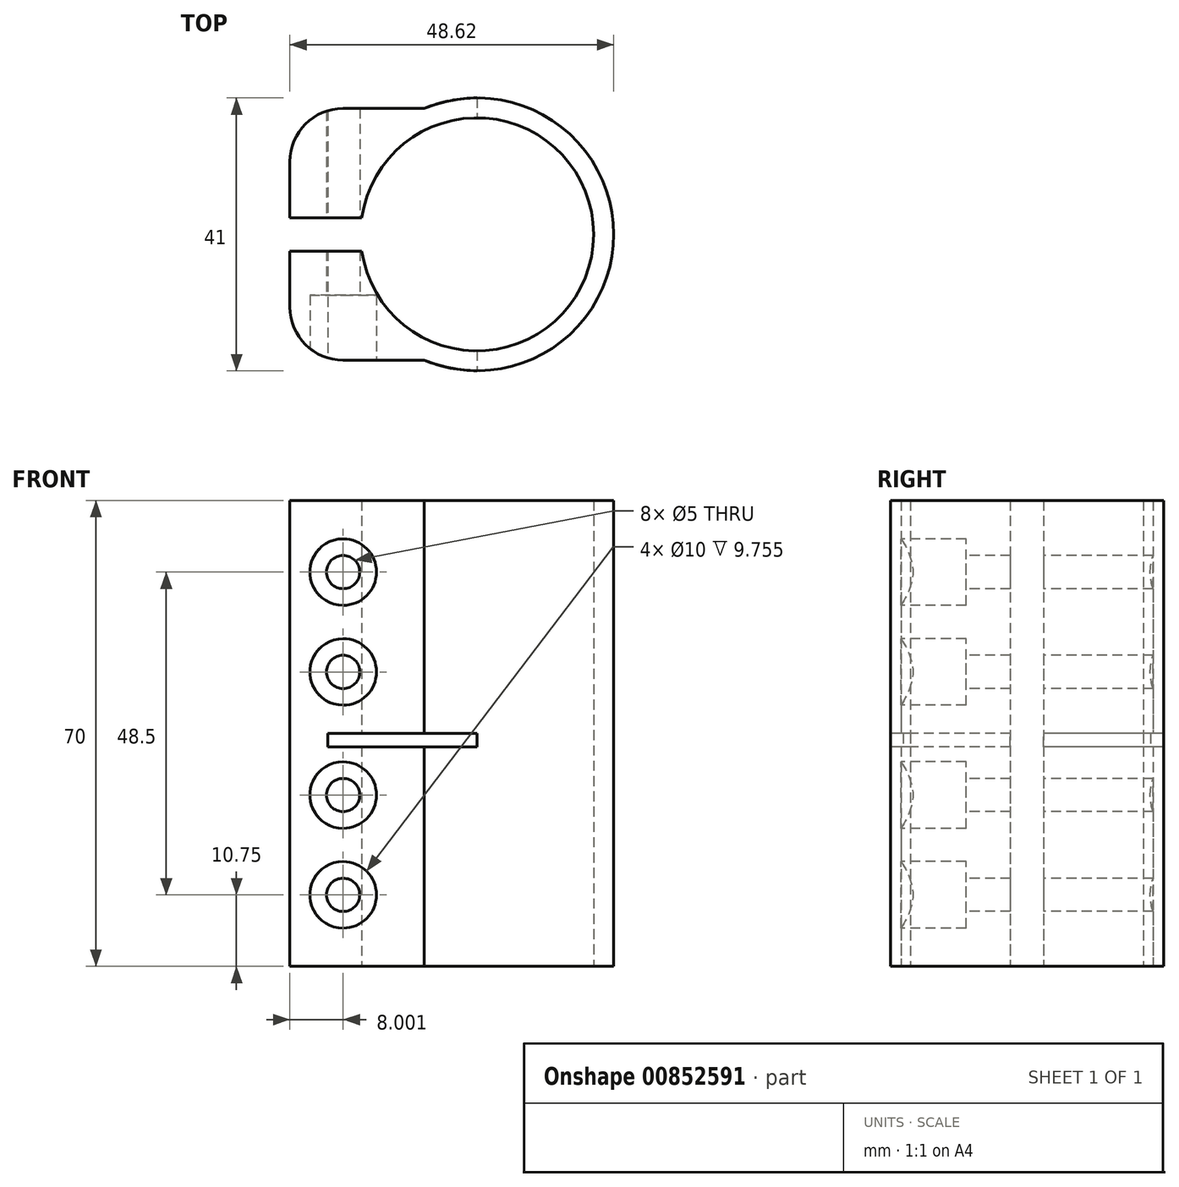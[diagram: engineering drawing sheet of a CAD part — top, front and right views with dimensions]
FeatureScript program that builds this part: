
annotation { "Feature Type Name" : "Feature", "Feature Type Description" : "" }
export const myFeature = defineFeature(function(context is Context, id is Id, definition is map)
    precondition{}
    {
        {
            var Q0;
            Q0=qCreatedBy(makeId("Top.planeOp"),FACE);
            var sketch = newSketch(context, id + "F0", { "sketchPlane" : qUnion([Q0])});
            skArc(sketch, "E0", {"start": v(-17.32, -2.5) * mm, "mid": v(17.5, 0) * mm, "end": v(-17.32, 2.5) * mm});
            skArc(sketch, "E1", {"start": v(-7.92, -18.9) * mm, "mid": v(20.5, 0) * mm, "end": v(-7.92, 18.9) * mm});
            skLineSegment(sketch, "E2", {"start": v(-7.92, 18.9) * mm, "end": v(-20.12, 18.9) * mm});
            skLineSegment(sketch, "E3", {"start": v(-28.12, 10.9) * mm, "end": v(-28.12, 2.5) * mm});
            skLineSegment(sketch, "E4", {"start": v(-28.12, 2.5) * mm, "end": v(-17.32, 2.5) * mm});
            skPoint(sketch, "E5.visualSharp", {"position": v(-28.12, 18.9) * mm});
            skArc(sketch, "E5.filletArc", {"start": v(-20.12, 18.9) * mm, "mid": v(-25.78, 16.57) * mm, "end": v(-28.12, 10.9) * mm});
            skLineSegment(sketch, "E6.MirrorCS", {"start": v(-28.12, -2.5) * mm, "end": v(-17.32, -2.5) * mm});
            skLineSegment(sketch, "E7.MirrorCS", {"start": v(-7.92, -18.9) * mm, "end": v(-20.12, -18.9) * mm});
            skLineSegment(sketch, "E8.MirrorCS", {"start": v(-28.12, -10.9) * mm, "end": v(-28.12, -2.5) * mm});
            skArc(sketch, "E9.MirrorCS", {"start": v(-20.12, -18.9) * mm, "mid": v(-25.78, -16.57) * mm, "end": v(-28.12, -10.9) * mm});
            skSolve(sketch);
        }
        {
            var Q0;
            Q0=makeQuery(id+"F0.imprint","IMPRINT",FACE,{"disambiguationData":[TD([[makeQuery(id+"F0.imprint","IMPRINT",EDGE,{"derivedFrom":sQuery(id+"F0.wireOp",EDGE,"E0")}),-1.0]])]});
            extrude(context, id + "F1", {"entities" : qUnion([Q0]), "endBound" : BoundingType.SYMMETRIC, "depth" : 70 * mm, "offsetDistance" : 25 * mm});
        }
        {
            var Q0;
            Q0=makeQuery(id+"F1.opExtrude","SWEPT_FACE",FACE,{"disambiguationData":[OSD([sQuery(id+"F0.wireOp",EDGE,"E7.MirrorCS")])]});
            var sketch = newSketch(context, id + "F2", { "sketchPlane" : qUnion([Q0])});
            skPoint(sketch, "E10", {"position": v(-20.12, 24.25) * mm});
            skPoint(sketch, "E11", {"position": v(-20.12, 9.25) * mm});
            skPoint(sketch, "E12", {"position": v(-20.12, -9.25) * mm});
            skPoint(sketch, "E13", {"position": v(-20.12, -24.25) * mm});
            skSolve(sketch);
        }
        {
            var Q0;
            Q0=sQuery(id+"F2.wireOp",VERTEX,"E10");
            var Q1;
            Q1=sQuery(id+"F2.wireOp",VERTEX,"E11");
            var Q2;
            Q2=sQuery(id+"F2.wireOp",VERTEX,"E12");
            var Q3;
            Q3=sQuery(id+"F2.wireOp",VERTEX,"E13");
            var Q4;
            Q4=makeQuery(id+"F1.opExtrude","SWEPT_BODY",BODY,{"disambiguationData":[OSD([sQuery(id+"F0.wireOp",EDGE,"E0"),sQuery(id+"F0.wireOp",EDGE,"E1"),sQuery(id+"F0.wireOp",EDGE,"E2"),sQuery(id+"F0.wireOp",EDGE,"E3"),sQuery(id+"F0.wireOp",EDGE,"E4"),sQuery(id+"F0.wireOp",EDGE,"E5.filletArc"),sQuery(id+"F0.wireOp",EDGE,"E6.MirrorCS"),sQuery(id+"F0.wireOp",EDGE,"E7.MirrorCS"),sQuery(id+"F0.wireOp",EDGE,"E8.MirrorCS"),sQuery(id+"F0.wireOp",EDGE,"E9.MirrorCS")])]});
            hole(context, id + "F3", {"style" : HoleStyle.C_BORE, "endStyle" : HoleEndStyle.THROUGH, "holeDiameter" : 5 * mm, "cBoreDiameter" : 10 * mm, "cBoreDepth" : 8 * mm, "majorDiameter" : 5 * mm, "isTappedThrough" : true, "tappedDepth" : 12 * mm, "tapClearance" : 3, "locations" : qUnion([Q0, Q1, Q2, Q3]), "scope" : qUnion([Q4])});
        }
        {
            var Q0;
            Q0=qCreatedBy(makeId("Front.planeOp"),FACE);
            var sketch = newSketch(context, id + "F4", { "sketchPlane" : qUnion([Q0])});
            skLineSegment(sketch, "E14.bottom", {"start": v(0, 0) * mm, "end": v(-22.4, 0) * mm});
            skLineSegment(sketch, "E14.top", {"start": v(0, -2) * mm, "end": v(-22.4, -2) * mm});
            skLineSegment(sketch, "E14.left", {"start": v(0, 0) * mm, "end": v(0, -2) * mm});
            skLineSegment(sketch, "E14.right", {"start": v(-22.4, 0) * mm, "end": v(-22.4, -2) * mm});
            skSolve(sketch);
        }
        {
            var Q0;
            Q0=makeQuery(id+"F4.imprint","IMPRINT",FACE,{"disambiguationData":[TD([[makeQuery(id+"F4.imprint","IMPRINT",EDGE,{"derivedFrom":sQuery(id+"F4.wireOp",EDGE,"E14.bottom")}),1.0]])]});
            extrude(context, id + "F5", {"entities" : qUnion([Q0]), "operationType" : NewBodyOperationType.REMOVE, "endBound" : BoundingType.SYMMETRIC, "oppositeDirection" : true, "depth" : 50 * mm, "offsetDistance" : 25 * mm});
        }
    });
